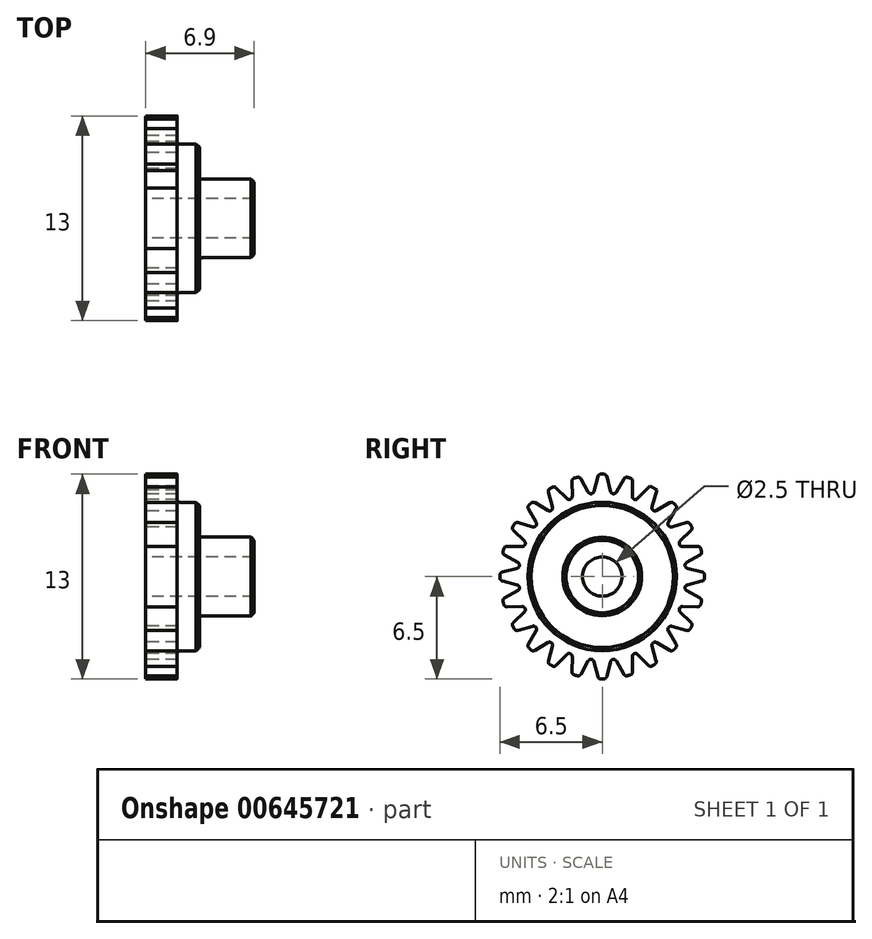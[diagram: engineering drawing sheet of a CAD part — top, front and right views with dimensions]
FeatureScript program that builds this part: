
annotation { "Feature Type Name" : "Feature", "Feature Type Description" : "" }
export const myFeature = defineFeature(function(context is Context, id is Id, definition is map)
    precondition{}
    {
        {
            var Q0;
            Q0=qCreatedBy(makeId("Front.planeOp"),FACE);
            var sketch = newSketch(context, id + "F0", { "sketchPlane" : qUnion([Q0])});
            skLineSegment(sketch, "E0", {"start": v(0, 1.25) * mm, "end": v(0, 6.5) * mm});
            skLineSegment(sketch, "E1", {"start": v(0, 6.5) * mm, "end": v(2, 6.5) * mm});
            skLineSegment(sketch, "E2", {"start": v(2, 6.5) * mm, "end": v(2, 4.72) * mm});
            skLineSegment(sketch, "E3", {"start": v(2, 4.71) * mm, "end": v(3.4, 4.72) * mm});
            skLineSegment(sketch, "E4", {"start": v(3.41, 4.72) * mm, "end": v(3.41, 2.5) * mm});
            skLineSegment(sketch, "E5", {"start": v(3.4, 2.5) * mm, "end": v(6.9, 2.5) * mm});
            skLineSegment(sketch, "E6", {"start": v(6.9, 2.5) * mm, "end": v(6.9, 1.25) * mm});
            skLineSegment(sketch, "E7", {"start": v(6.9, 1.25) * mm, "end": v(0, 1.25) * mm});
            skLineSegment(sketch, "E8", {"start": v(0, 0) * mm, "end": v(11.79, 0) * mm, "construction": true});
            skSolve(sketch);
        }
        {
            var Q0;
            Q0=makeQuery(id+"F0.imprint","IMPRINT",FACE,{"disambiguationData":[TD([[makeQuery(id+"F0.imprint","IMPRINT",EDGE,{"derivedFrom":sQuery(id+"F0.wireOp",EDGE,"E0")}),-1.0]])]});
            var Q1;
            Q1=sQuery(id+"F0.wireOp",EDGE,"E8");
            revolve(context, id + "F1", {"entities" : qUnion([Q0]), "axis" : qUnion([Q1]), "revolveType" : RevolveType.FULL});
        }
        {
            var Q0;
            Q0=makeQuery(id+"F1.opRevolve","SWEPT_FACE",FACE,{"disambiguationData":[OSD([sQuery(id+"F0.wireOp",EDGE,"E0")])]});
            var sketch = newSketch(context, id + "F2", { "sketchPlane" : qUnion([Q0])});
            skLineSegment(sketch, "E9", {"start": v(-0.25, 6.5) * mm, "end": v(-0.66, 4.87) * mm});
            skArc(sketch, "E10", {"start": v(0.25, 6.5) * mm, "mid": v(0, 6.5) * mm, "end": v(-0.25, 6.5) * mm});
            skLineSegment(sketch, "E11.MirrorCS", {"start": v(0.25, 6.5) * mm, "end": v(0.66, 4.87) * mm});
            skLineSegment(sketch, "E12.1.0", {"start": v(-1.92, 6.2) * mm, "end": v(-1.9, 4.53) * mm});
            skArc(sketch, "E12.1.1", {"start": v(-1.44, 6.34) * mm, "mid": v(-1.68, 6.28) * mm, "end": v(-1.92, 6.2) * mm});
            skLineSegment(sketch, "E12.1.2", {"start": v(-1.44, 6.34) * mm, "end": v(-0.62, 4.87) * mm});
            skLineSegment(sketch, "E12.2.0", {"start": v(-3.46, 5.5) * mm, "end": v(-3, 3.89) * mm});
            skArc(sketch, "E12.2.1", {"start": v(-3.03, 5.75) * mm, "mid": v(-3.25, 5.63) * mm, "end": v(-3.46, 5.5) * mm});
            skLineSegment(sketch, "E12.2.2", {"start": v(-3.03, 5.75) * mm, "end": v(-1.86, 4.55) * mm});
            skLineSegment(sketch, "E12.3.0", {"start": v(-4.77, 4.42) * mm, "end": v(-3.91, 2.97) * mm});
            skArc(sketch, "E12.3.1", {"start": v(-4.42, 4.77) * mm, "mid": v(-4.6, 4.6) * mm, "end": v(-4.77, 4.42) * mm});
            skLineSegment(sketch, "E12.3.2", {"start": v(-4.42, 4.77) * mm, "end": v(-2.97, 3.91) * mm});
            skLineSegment(sketch, "E12.4.0", {"start": v(-5.75, 3.03) * mm, "end": v(-4.55, 1.86) * mm});
            skArc(sketch, "E12.4.1", {"start": v(-5.5, 3.46) * mm, "mid": v(-5.63, 3.25) * mm, "end": v(-5.75, 3.03) * mm});
            skLineSegment(sketch, "E12.4.2", {"start": v(-5.5, 3.46) * mm, "end": v(-3.89, 3) * mm});
            skLineSegment(sketch, "E12.5.0", {"start": v(-6.34, 1.44) * mm, "end": v(-4.87, 0.62) * mm});
            skArc(sketch, "E12.5.1", {"start": v(-6.2, 1.92) * mm, "mid": v(-6.28, 1.68) * mm, "end": v(-6.34, 1.44) * mm});
            skLineSegment(sketch, "E12.5.2", {"start": v(-6.2, 1.92) * mm, "end": v(-4.53, 1.9) * mm});
            skLineSegment(sketch, "E12.6.0", {"start": v(-6.5, -0.25) * mm, "end": v(-4.87, -0.66) * mm});
            skArc(sketch, "E12.6.1", {"start": v(-6.5, 0.25) * mm, "mid": v(-6.5, 0) * mm, "end": v(-6.5, -0.25) * mm});
            skLineSegment(sketch, "E12.6.2", {"start": v(-6.5, 0.25) * mm, "end": v(-4.87, 0.66) * mm});
            skLineSegment(sketch, "E12.7.0", {"start": v(-6.2, -1.92) * mm, "end": v(-4.53, -1.9) * mm});
            skArc(sketch, "E12.7.1", {"start": v(-6.34, -1.44) * mm, "mid": v(-6.28, -1.68) * mm, "end": v(-6.2, -1.92) * mm});
            skLineSegment(sketch, "E12.7.2", {"start": v(-6.34, -1.44) * mm, "end": v(-4.87, -0.62) * mm});
            skLineSegment(sketch, "E12.8.0", {"start": v(-5.5, -3.46) * mm, "end": v(-3.89, -3) * mm});
            skArc(sketch, "E12.8.1", {"start": v(-5.75, -3.03) * mm, "mid": v(-5.63, -3.25) * mm, "end": v(-5.5, -3.46) * mm});
            skLineSegment(sketch, "E12.8.2", {"start": v(-5.75, -3.03) * mm, "end": v(-4.55, -1.86) * mm});
            skLineSegment(sketch, "E12.9.0", {"start": v(-4.42, -4.77) * mm, "end": v(-2.97, -3.91) * mm});
            skArc(sketch, "E12.9.1", {"start": v(-4.77, -4.42) * mm, "mid": v(-4.6, -4.6) * mm, "end": v(-4.42, -4.77) * mm});
            skLineSegment(sketch, "E12.9.2", {"start": v(-4.77, -4.42) * mm, "end": v(-3.91, -2.97) * mm});
            skLineSegment(sketch, "E12.10.0", {"start": v(-3.03, -5.75) * mm, "end": v(-1.86, -4.55) * mm});
            skArc(sketch, "E12.10.1", {"start": v(-3.46, -5.5) * mm, "mid": v(-3.25, -5.63) * mm, "end": v(-3.03, -5.75) * mm});
            skLineSegment(sketch, "E12.10.2", {"start": v(-3.46, -5.5) * mm, "end": v(-3, -3.89) * mm});
            skLineSegment(sketch, "E12.11.0", {"start": v(-1.44, -6.34) * mm, "end": v(-0.62, -4.87) * mm});
            skArc(sketch, "E12.11.1", {"start": v(-1.92, -6.2) * mm, "mid": v(-1.68, -6.28) * mm, "end": v(-1.44, -6.34) * mm});
            skLineSegment(sketch, "E12.11.2", {"start": v(-1.92, -6.2) * mm, "end": v(-1.9, -4.53) * mm});
            skLineSegment(sketch, "E12.12.0", {"start": v(0.25, -6.5) * mm, "end": v(0.66, -4.87) * mm});
            skArc(sketch, "E12.12.1", {"start": v(-0.25, -6.5) * mm, "mid": v(0, -6.5) * mm, "end": v(0.25, -6.5) * mm});
            skLineSegment(sketch, "E12.12.2", {"start": v(-0.25, -6.5) * mm, "end": v(-0.66, -4.87) * mm});
            skLineSegment(sketch, "E12.13.0", {"start": v(1.92, -6.2) * mm, "end": v(1.9, -4.53) * mm});
            skArc(sketch, "E12.13.1", {"start": v(1.44, -6.34) * mm, "mid": v(1.68, -6.28) * mm, "end": v(1.92, -6.2) * mm});
            skLineSegment(sketch, "E12.13.2", {"start": v(1.44, -6.34) * mm, "end": v(0.62, -4.87) * mm});
            skLineSegment(sketch, "E12.14.0", {"start": v(3.46, -5.5) * mm, "end": v(3, -3.89) * mm});
            skArc(sketch, "E12.14.1", {"start": v(3.03, -5.75) * mm, "mid": v(3.25, -5.63) * mm, "end": v(3.46, -5.5) * mm});
            skLineSegment(sketch, "E12.14.2", {"start": v(3.03, -5.75) * mm, "end": v(1.86, -4.55) * mm});
            skLineSegment(sketch, "E12.15.0", {"start": v(4.77, -4.42) * mm, "end": v(3.91, -2.97) * mm});
            skArc(sketch, "E12.15.1", {"start": v(4.42, -4.77) * mm, "mid": v(4.6, -4.6) * mm, "end": v(4.77, -4.42) * mm});
            skLineSegment(sketch, "E12.15.2", {"start": v(4.42, -4.77) * mm, "end": v(2.97, -3.91) * mm});
            skLineSegment(sketch, "E12.16.0", {"start": v(5.75, -3.03) * mm, "end": v(4.55, -1.86) * mm});
            skArc(sketch, "E12.16.1", {"start": v(5.5, -3.46) * mm, "mid": v(5.63, -3.25) * mm, "end": v(5.75, -3.03) * mm});
            skLineSegment(sketch, "E12.16.2", {"start": v(5.5, -3.46) * mm, "end": v(3.89, -3) * mm});
            skLineSegment(sketch, "E12.17.0", {"start": v(6.34, -1.44) * mm, "end": v(4.87, -0.62) * mm});
            skArc(sketch, "E12.17.1", {"start": v(6.2, -1.92) * mm, "mid": v(6.28, -1.68) * mm, "end": v(6.34, -1.44) * mm});
            skLineSegment(sketch, "E12.17.2", {"start": v(6.2, -1.92) * mm, "end": v(4.53, -1.9) * mm});
            skLineSegment(sketch, "E12.18.0", {"start": v(6.5, 0.25) * mm, "end": v(4.87, 0.66) * mm});
            skArc(sketch, "E12.18.1", {"start": v(6.5, -0.25) * mm, "mid": v(6.5, 0) * mm, "end": v(6.5, 0.25) * mm});
            skLineSegment(sketch, "E12.18.2", {"start": v(6.5, -0.25) * mm, "end": v(4.87, -0.66) * mm});
            skLineSegment(sketch, "E12.19.0", {"start": v(6.2, 1.92) * mm, "end": v(4.53, 1.9) * mm});
            skArc(sketch, "E12.19.1", {"start": v(6.34, 1.44) * mm, "mid": v(6.28, 1.68) * mm, "end": v(6.2, 1.92) * mm});
            skLineSegment(sketch, "E12.19.2", {"start": v(6.34, 1.44) * mm, "end": v(4.87, 0.62) * mm});
            skLineSegment(sketch, "E12.20.0", {"start": v(5.5, 3.46) * mm, "end": v(3.89, 3) * mm});
            skArc(sketch, "E12.20.1", {"start": v(5.75, 3.03) * mm, "mid": v(5.63, 3.25) * mm, "end": v(5.5, 3.46) * mm});
            skLineSegment(sketch, "E12.20.2", {"start": v(5.75, 3.03) * mm, "end": v(4.55, 1.86) * mm});
            skLineSegment(sketch, "E12.21.0", {"start": v(4.42, 4.77) * mm, "end": v(2.97, 3.91) * mm});
            skArc(sketch, "E12.21.1", {"start": v(4.77, 4.42) * mm, "mid": v(4.6, 4.6) * mm, "end": v(4.42, 4.77) * mm});
            skLineSegment(sketch, "E12.21.2", {"start": v(4.77, 4.42) * mm, "end": v(3.91, 2.97) * mm});
            skLineSegment(sketch, "E12.22.0", {"start": v(3.03, 5.75) * mm, "end": v(1.86, 4.55) * mm});
            skArc(sketch, "E12.22.1", {"start": v(3.46, 5.5) * mm, "mid": v(3.25, 5.63) * mm, "end": v(3.03, 5.75) * mm});
            skLineSegment(sketch, "E12.22.2", {"start": v(3.46, 5.5) * mm, "end": v(3, 3.89) * mm});
            skLineSegment(sketch, "E12.23.0", {"start": v(1.44, 6.34) * mm, "end": v(0.62, 4.87) * mm});
            skArc(sketch, "E12.23.1", {"start": v(1.92, 6.2) * mm, "mid": v(1.68, 6.28) * mm, "end": v(1.44, 6.34) * mm});
            skLineSegment(sketch, "E12.23.2", {"start": v(1.92, 6.2) * mm, "end": v(1.9, 4.53) * mm});
            skCircle(sketch, "E13", {"center": v(0, 0) * mm, "radius": 7.21 * mm});
            skSolve(sketch);
        }
        {
            var Q0;
            {var subQ0=sQuery(id+"F2.wireOp",EDGE,"E12.2.0");var subQ3=sQuery(id+"F2.wireOp",EDGE,"E12.3.2");var subQ4=makeQuery(id+"F2.imprint","INTERSECT",VERTEX,{"derivedFrom":[subQ0,subQ3]});Q0=makeQuery(id+"F2.imprint","IMPRINT",FACE,{"disambiguationData":[TD([[makeQuery(id+"F2.imprint","IMPRINT",EDGE,{"disambiguationData":[TD([[subQ4,1.0]])],"derivedFrom":subQ0}),-1.0]])]});}
            var Q1;
            {var subQ0=sQuery(id+"F2.wireOp",EDGE,"E12.1.0");var subQ3=sQuery(id+"F2.wireOp",EDGE,"E12.2.2");var subQ4=makeQuery(id+"F2.imprint","INTERSECT",VERTEX,{"derivedFrom":[subQ0,subQ3]});Q1=makeQuery(id+"F2.imprint","IMPRINT",FACE,{"disambiguationData":[TD([[makeQuery(id+"F2.imprint","IMPRINT",EDGE,{"disambiguationData":[TD([[subQ4,1.0]])],"derivedFrom":subQ0}),-1.0]])]});}
            var Q2;
            {var subQ0=sQuery(id+"F2.wireOp",EDGE,"E9");var subQ3=sQuery(id+"F2.wireOp",EDGE,"E12.1.2");var subQ4=makeQuery(id+"F2.imprint","INTERSECT",VERTEX,{"derivedFrom":[subQ0,subQ3]});Q2=makeQuery(id+"F2.imprint","IMPRINT",FACE,{"disambiguationData":[TD([[makeQuery(id+"F2.imprint","IMPRINT",EDGE,{"disambiguationData":[TD([[subQ4,1.0]])],"derivedFrom":subQ0}),-1.0]])]});}
            var Q3;
            {var subQ0=sQuery(id+"F2.wireOp",EDGE,"E11.MirrorCS");var subQ3=sQuery(id+"F2.wireOp",EDGE,"E12.23.0");var subQ4=makeQuery(id+"F2.imprint","INTERSECT",VERTEX,{"derivedFrom":[subQ0,subQ3]});Q3=makeQuery(id+"F2.imprint","IMPRINT",FACE,{"disambiguationData":[TD([[makeQuery(id+"F2.imprint","IMPRINT",EDGE,{"disambiguationData":[TD([[subQ4,1.0]])],"derivedFrom":subQ0}),1.0]])]});}
            var Q4;
            {var subQ0=sQuery(id+"F2.wireOp",EDGE,"E12.22.0");var subQ3=sQuery(id+"F2.wireOp",EDGE,"E12.23.2");var subQ4=makeQuery(id+"F2.imprint","INTERSECT",VERTEX,{"derivedFrom":[subQ0,subQ3]});Q4=makeQuery(id+"F2.imprint","IMPRINT",FACE,{"disambiguationData":[TD([[makeQuery(id+"F2.imprint","IMPRINT",EDGE,{"disambiguationData":[TD([[subQ4,1.0]])],"derivedFrom":subQ0}),-1.0]])]});}
            var Q5;
            {var subQ0=sQuery(id+"F2.wireOp",EDGE,"E12.21.0");var subQ3=sQuery(id+"F2.wireOp",EDGE,"E12.22.2");var subQ4=makeQuery(id+"F2.imprint","INTERSECT",VERTEX,{"derivedFrom":[subQ0,subQ3]});Q5=makeQuery(id+"F2.imprint","IMPRINT",FACE,{"disambiguationData":[TD([[makeQuery(id+"F2.imprint","IMPRINT",EDGE,{"disambiguationData":[TD([[subQ4,1.0]])],"derivedFrom":subQ0}),-1.0]])]});}
            var Q6;
            {var subQ0=sQuery(id+"F2.wireOp",EDGE,"E12.20.0");var subQ3=sQuery(id+"F2.wireOp",EDGE,"E12.21.2");var subQ4=makeQuery(id+"F2.imprint","INTERSECT",VERTEX,{"derivedFrom":[subQ0,subQ3]});Q6=makeQuery(id+"F2.imprint","IMPRINT",FACE,{"disambiguationData":[TD([[makeQuery(id+"F2.imprint","IMPRINT",EDGE,{"disambiguationData":[TD([[subQ4,1.0]])],"derivedFrom":subQ0}),-1.0]])]});}
            var Q7;
            {var subQ0=sQuery(id+"F2.wireOp",EDGE,"E12.19.0");var subQ3=sQuery(id+"F2.wireOp",EDGE,"E12.20.2");var subQ4=makeQuery(id+"F2.imprint","INTERSECT",VERTEX,{"derivedFrom":[subQ0,subQ3]});Q7=makeQuery(id+"F2.imprint","IMPRINT",FACE,{"disambiguationData":[TD([[makeQuery(id+"F2.imprint","IMPRINT",EDGE,{"disambiguationData":[TD([[subQ4,1.0]])],"derivedFrom":subQ0}),-1.0]])]});}
            var Q8;
            {var subQ0=sQuery(id+"F2.wireOp",EDGE,"E12.18.0");var subQ3=sQuery(id+"F2.wireOp",EDGE,"E12.19.2");var subQ4=makeQuery(id+"F2.imprint","INTERSECT",VERTEX,{"derivedFrom":[subQ0,subQ3]});Q8=makeQuery(id+"F2.imprint","IMPRINT",FACE,{"disambiguationData":[TD([[makeQuery(id+"F2.imprint","IMPRINT",EDGE,{"disambiguationData":[TD([[subQ4,1.0]])],"derivedFrom":subQ0}),-1.0]])]});}
            var Q9;
            {var subQ0=sQuery(id+"F2.wireOp",EDGE,"E12.17.0");var subQ3=sQuery(id+"F2.wireOp",EDGE,"E12.18.2");var subQ4=makeQuery(id+"F2.imprint","INTERSECT",VERTEX,{"derivedFrom":[subQ0,subQ3]});Q9=makeQuery(id+"F2.imprint","IMPRINT",FACE,{"disambiguationData":[TD([[makeQuery(id+"F2.imprint","IMPRINT",EDGE,{"disambiguationData":[TD([[subQ4,1.0]])],"derivedFrom":subQ0}),-1.0]])]});}
            var Q10;
            {var subQ0=sQuery(id+"F2.wireOp",EDGE,"E12.16.0");var subQ3=sQuery(id+"F2.wireOp",EDGE,"E12.17.2");var subQ4=makeQuery(id+"F2.imprint","INTERSECT",VERTEX,{"derivedFrom":[subQ0,subQ3]});Q10=makeQuery(id+"F2.imprint","IMPRINT",FACE,{"disambiguationData":[TD([[makeQuery(id+"F2.imprint","IMPRINT",EDGE,{"disambiguationData":[TD([[subQ4,1.0]])],"derivedFrom":subQ0}),-1.0]])]});}
            var Q11;
            {var subQ0=sQuery(id+"F2.wireOp",EDGE,"E12.15.0");var subQ3=sQuery(id+"F2.wireOp",EDGE,"E12.16.2");var subQ4=makeQuery(id+"F2.imprint","INTERSECT",VERTEX,{"derivedFrom":[subQ0,subQ3]});Q11=makeQuery(id+"F2.imprint","IMPRINT",FACE,{"disambiguationData":[TD([[makeQuery(id+"F2.imprint","IMPRINT",EDGE,{"disambiguationData":[TD([[subQ4,1.0]])],"derivedFrom":subQ0}),-1.0]])]});}
            var Q12;
            {var subQ0=sQuery(id+"F2.wireOp",EDGE,"E12.14.0");var subQ3=sQuery(id+"F2.wireOp",EDGE,"E12.15.2");var subQ4=makeQuery(id+"F2.imprint","INTERSECT",VERTEX,{"derivedFrom":[subQ0,subQ3]});Q12=makeQuery(id+"F2.imprint","IMPRINT",FACE,{"disambiguationData":[TD([[makeQuery(id+"F2.imprint","IMPRINT",EDGE,{"disambiguationData":[TD([[subQ4,1.0]])],"derivedFrom":subQ0}),-1.0]])]});}
            var Q13;
            {var subQ0=sQuery(id+"F2.wireOp",EDGE,"E12.13.0");var subQ3=sQuery(id+"F2.wireOp",EDGE,"E12.14.2");var subQ4=makeQuery(id+"F2.imprint","INTERSECT",VERTEX,{"derivedFrom":[subQ0,subQ3]});Q13=makeQuery(id+"F2.imprint","IMPRINT",FACE,{"disambiguationData":[TD([[makeQuery(id+"F2.imprint","IMPRINT",EDGE,{"disambiguationData":[TD([[subQ4,1.0]])],"derivedFrom":subQ0}),-1.0]])]});}
            var Q14;
            {var subQ0=sQuery(id+"F2.wireOp",EDGE,"E12.12.0");var subQ3=sQuery(id+"F2.wireOp",EDGE,"E12.13.2");var subQ4=makeQuery(id+"F2.imprint","INTERSECT",VERTEX,{"derivedFrom":[subQ0,subQ3]});Q14=makeQuery(id+"F2.imprint","IMPRINT",FACE,{"disambiguationData":[TD([[makeQuery(id+"F2.imprint","IMPRINT",EDGE,{"disambiguationData":[TD([[subQ4,1.0]])],"derivedFrom":subQ0}),-1.0]])]});}
            var Q15;
            {var subQ0=sQuery(id+"F2.wireOp",EDGE,"E12.11.0");var subQ3=sQuery(id+"F2.wireOp",EDGE,"E12.12.2");var subQ4=makeQuery(id+"F2.imprint","INTERSECT",VERTEX,{"derivedFrom":[subQ0,subQ3]});Q15=makeQuery(id+"F2.imprint","IMPRINT",FACE,{"disambiguationData":[TD([[makeQuery(id+"F2.imprint","IMPRINT",EDGE,{"disambiguationData":[TD([[subQ4,1.0]])],"derivedFrom":subQ0}),-1.0]])]});}
            var Q16;
            {var subQ0=sQuery(id+"F2.wireOp",EDGE,"E12.10.0");var subQ3=sQuery(id+"F2.wireOp",EDGE,"E12.11.2");var subQ4=makeQuery(id+"F2.imprint","INTERSECT",VERTEX,{"derivedFrom":[subQ0,subQ3]});Q16=makeQuery(id+"F2.imprint","IMPRINT",FACE,{"disambiguationData":[TD([[makeQuery(id+"F2.imprint","IMPRINT",EDGE,{"disambiguationData":[TD([[subQ4,1.0]])],"derivedFrom":subQ0}),-1.0]])]});}
            var Q17;
            {var subQ0=sQuery(id+"F2.wireOp",EDGE,"E12.9.0");var subQ3=sQuery(id+"F2.wireOp",EDGE,"E12.10.2");var subQ4=makeQuery(id+"F2.imprint","INTERSECT",VERTEX,{"derivedFrom":[subQ0,subQ3]});Q17=makeQuery(id+"F2.imprint","IMPRINT",FACE,{"disambiguationData":[TD([[makeQuery(id+"F2.imprint","IMPRINT",EDGE,{"disambiguationData":[TD([[subQ4,1.0]])],"derivedFrom":subQ0}),-1.0]])]});}
            var Q18;
            {var subQ0=sQuery(id+"F2.wireOp",EDGE,"E12.8.0");var subQ3=sQuery(id+"F2.wireOp",EDGE,"E12.9.2");var subQ4=makeQuery(id+"F2.imprint","INTERSECT",VERTEX,{"derivedFrom":[subQ0,subQ3]});Q18=makeQuery(id+"F2.imprint","IMPRINT",FACE,{"disambiguationData":[TD([[makeQuery(id+"F2.imprint","IMPRINT",EDGE,{"disambiguationData":[TD([[subQ4,1.0]])],"derivedFrom":subQ0}),-1.0]])]});}
            var Q19;
            {var subQ0=sQuery(id+"F2.wireOp",EDGE,"E12.7.0");var subQ3=sQuery(id+"F2.wireOp",EDGE,"E12.8.2");var subQ4=makeQuery(id+"F2.imprint","INTERSECT",VERTEX,{"derivedFrom":[subQ0,subQ3]});Q19=makeQuery(id+"F2.imprint","IMPRINT",FACE,{"disambiguationData":[TD([[makeQuery(id+"F2.imprint","IMPRINT",EDGE,{"disambiguationData":[TD([[subQ4,1.0]])],"derivedFrom":subQ0}),-1.0]])]});}
            var Q20;
            {var subQ0=sQuery(id+"F2.wireOp",EDGE,"E12.6.0");var subQ3=sQuery(id+"F2.wireOp",EDGE,"E12.7.2");var subQ4=makeQuery(id+"F2.imprint","INTERSECT",VERTEX,{"derivedFrom":[subQ0,subQ3]});Q20=makeQuery(id+"F2.imprint","IMPRINT",FACE,{"disambiguationData":[TD([[makeQuery(id+"F2.imprint","IMPRINT",EDGE,{"disambiguationData":[TD([[subQ4,1.0]])],"derivedFrom":subQ0}),-1.0]])]});}
            var Q21;
            {var subQ0=sQuery(id+"F2.wireOp",EDGE,"E12.5.0");var subQ3=sQuery(id+"F2.wireOp",EDGE,"E12.6.2");var subQ4=makeQuery(id+"F2.imprint","INTERSECT",VERTEX,{"derivedFrom":[subQ0,subQ3]});Q21=makeQuery(id+"F2.imprint","IMPRINT",FACE,{"disambiguationData":[TD([[makeQuery(id+"F2.imprint","IMPRINT",EDGE,{"disambiguationData":[TD([[subQ4,1.0]])],"derivedFrom":subQ0}),-1.0]])]});}
            var Q22;
            {var subQ0=sQuery(id+"F2.wireOp",EDGE,"E12.4.0");var subQ3=sQuery(id+"F2.wireOp",EDGE,"E12.5.2");var subQ4=makeQuery(id+"F2.imprint","INTERSECT",VERTEX,{"derivedFrom":[subQ0,subQ3]});Q22=makeQuery(id+"F2.imprint","IMPRINT",FACE,{"disambiguationData":[TD([[makeQuery(id+"F2.imprint","IMPRINT",EDGE,{"disambiguationData":[TD([[subQ4,1.0]])],"derivedFrom":subQ0}),-1.0]])]});}
            var Q23;
            {var subQ0=sQuery(id+"F2.wireOp",EDGE,"E12.3.0");var subQ3=sQuery(id+"F2.wireOp",EDGE,"E12.4.2");var subQ4=makeQuery(id+"F2.imprint","INTERSECT",VERTEX,{"derivedFrom":[subQ0,subQ3]});Q23=makeQuery(id+"F2.imprint","IMPRINT",FACE,{"disambiguationData":[TD([[makeQuery(id+"F2.imprint","IMPRINT",EDGE,{"disambiguationData":[TD([[subQ4,1.0]])],"derivedFrom":subQ0}),-1.0]])]});}
            extrude(context, id + "F3", {"entities" : qUnion([Q0, Q1, Q2, Q3, Q4, Q5, Q6, Q7, Q8, Q9, Q10, Q11, Q12, Q13, Q14, Q15, Q16, Q17, Q18, Q19, Q20, Q21, Q22, Q23]), "operationType" : NewBodyOperationType.REMOVE, "oppositeDirection" : true, "depth" : 25 * mm, "offsetDistance" : 25 * mm});
        }
        {
            var Q0;
            Q0=makeQuery(id+"F3.boolean.opBoolean","COPY",EDGE,{"derivedFrom":makeQuery(id+"F3.opExtrude","SWEPT_EDGE",EDGE,{"disambiguationData":[OSD([sQuery(id+"F2.wireOp",EDGE,"E12.2.0"),sQuery(id+"F2.wireOp",EDGE,"E12.3.2")])]})});
            var Q1;
            Q1=makeQuery(id+"F3.boolean.opBoolean","COPY",EDGE,{"derivedFrom":makeQuery(id+"F3.opExtrude","SWEPT_EDGE",EDGE,{"disambiguationData":[OSD([sQuery(id+"F2.wireOp",EDGE,"E12.1.0"),sQuery(id+"F2.wireOp",EDGE,"E12.2.2")])]})});
            var Q2;
            Q2=makeQuery(id+"F3.boolean.opBoolean","COPY",EDGE,{"derivedFrom":makeQuery(id+"F3.opExtrude","SWEPT_EDGE",EDGE,{"disambiguationData":[OSD([sQuery(id+"F2.wireOp",EDGE,"E9"),sQuery(id+"F2.wireOp",EDGE,"E12.1.2")])]})});
            var Q3;
            Q3=makeQuery(id+"F3.boolean.opBoolean","COPY",EDGE,{"derivedFrom":makeQuery(id+"F3.opExtrude","SWEPT_EDGE",EDGE,{"disambiguationData":[OSD([sQuery(id+"F2.wireOp",EDGE,"E11.MirrorCS"),sQuery(id+"F2.wireOp",EDGE,"E12.23.0")])]})});
            var Q4;
            Q4=makeQuery(id+"F3.boolean.opBoolean","COPY",EDGE,{"derivedFrom":makeQuery(id+"F3.opExtrude","SWEPT_EDGE",EDGE,{"disambiguationData":[OSD([sQuery(id+"F2.wireOp",EDGE,"E12.22.0"),sQuery(id+"F2.wireOp",EDGE,"E12.23.2")])]})});
            var Q5;
            Q5=makeQuery(id+"F3.boolean.opBoolean","COPY",EDGE,{"derivedFrom":makeQuery(id+"F3.opExtrude","SWEPT_EDGE",EDGE,{"disambiguationData":[OSD([sQuery(id+"F2.wireOp",EDGE,"E12.21.0"),sQuery(id+"F2.wireOp",EDGE,"E12.22.2")])]})});
            var Q6;
            Q6=makeQuery(id+"F3.boolean.opBoolean","COPY",EDGE,{"derivedFrom":makeQuery(id+"F3.opExtrude","SWEPT_EDGE",EDGE,{"disambiguationData":[OSD([sQuery(id+"F2.wireOp",EDGE,"E12.20.0"),sQuery(id+"F2.wireOp",EDGE,"E12.21.2")])]})});
            var Q7;
            Q7=makeQuery(id+"F3.boolean.opBoolean","COPY",EDGE,{"derivedFrom":makeQuery(id+"F3.opExtrude","SWEPT_EDGE",EDGE,{"disambiguationData":[OSD([sQuery(id+"F2.wireOp",EDGE,"E12.19.0"),sQuery(id+"F2.wireOp",EDGE,"E12.20.2")])]})});
            var Q8;
            Q8=makeQuery(id+"F3.boolean.opBoolean","COPY",EDGE,{"derivedFrom":makeQuery(id+"F3.opExtrude","SWEPT_EDGE",EDGE,{"disambiguationData":[OSD([sQuery(id+"F2.wireOp",EDGE,"E12.18.0"),sQuery(id+"F2.wireOp",EDGE,"E12.19.2")])]})});
            var Q9;
            Q9=makeQuery(id+"F3.boolean.opBoolean","COPY",EDGE,{"derivedFrom":makeQuery(id+"F3.opExtrude","SWEPT_EDGE",EDGE,{"disambiguationData":[OSD([sQuery(id+"F2.wireOp",EDGE,"E12.17.0"),sQuery(id+"F2.wireOp",EDGE,"E12.18.2")])]})});
            var Q10;
            Q10=makeQuery(id+"F3.boolean.opBoolean","COPY",EDGE,{"derivedFrom":makeQuery(id+"F3.opExtrude","SWEPT_EDGE",EDGE,{"disambiguationData":[OSD([sQuery(id+"F2.wireOp",EDGE,"E12.16.0"),sQuery(id+"F2.wireOp",EDGE,"E12.17.2")])]})});
            var Q11;
            Q11=makeQuery(id+"F3.boolean.opBoolean","COPY",EDGE,{"derivedFrom":makeQuery(id+"F3.opExtrude","SWEPT_EDGE",EDGE,{"disambiguationData":[OSD([sQuery(id+"F2.wireOp",EDGE,"E12.15.0"),sQuery(id+"F2.wireOp",EDGE,"E12.16.2")])]})});
            var Q12;
            Q12=makeQuery(id+"F3.boolean.opBoolean","COPY",EDGE,{"derivedFrom":makeQuery(id+"F3.opExtrude","SWEPT_EDGE",EDGE,{"disambiguationData":[OSD([sQuery(id+"F2.wireOp",EDGE,"E12.14.0"),sQuery(id+"F2.wireOp",EDGE,"E12.15.2")])]})});
            var Q13;
            Q13=makeQuery(id+"F3.boolean.opBoolean","COPY",EDGE,{"derivedFrom":makeQuery(id+"F3.opExtrude","SWEPT_EDGE",EDGE,{"disambiguationData":[OSD([sQuery(id+"F2.wireOp",EDGE,"E12.13.0"),sQuery(id+"F2.wireOp",EDGE,"E12.14.2")])]})});
            var Q14;
            Q14=makeQuery(id+"F3.boolean.opBoolean","COPY",EDGE,{"derivedFrom":makeQuery(id+"F3.opExtrude","SWEPT_EDGE",EDGE,{"disambiguationData":[OSD([sQuery(id+"F2.wireOp",EDGE,"E12.12.0"),sQuery(id+"F2.wireOp",EDGE,"E12.13.2")])]})});
            var Q15;
            Q15=makeQuery(id+"F3.boolean.opBoolean","COPY",EDGE,{"derivedFrom":makeQuery(id+"F3.opExtrude","SWEPT_EDGE",EDGE,{"disambiguationData":[OSD([sQuery(id+"F2.wireOp",EDGE,"E12.11.0"),sQuery(id+"F2.wireOp",EDGE,"E12.12.2")])]})});
            var Q16;
            Q16=makeQuery(id+"F3.boolean.opBoolean","COPY",EDGE,{"derivedFrom":makeQuery(id+"F3.opExtrude","SWEPT_EDGE",EDGE,{"disambiguationData":[OSD([sQuery(id+"F2.wireOp",EDGE,"E12.10.0"),sQuery(id+"F2.wireOp",EDGE,"E12.11.2")])]})});
            var Q17;
            Q17=makeQuery(id+"F3.boolean.opBoolean","COPY",EDGE,{"derivedFrom":makeQuery(id+"F3.opExtrude","SWEPT_EDGE",EDGE,{"disambiguationData":[OSD([sQuery(id+"F2.wireOp",EDGE,"E12.9.0"),sQuery(id+"F2.wireOp",EDGE,"E12.10.2")])]})});
            var Q18;
            Q18=makeQuery(id+"F3.boolean.opBoolean","COPY",EDGE,{"derivedFrom":makeQuery(id+"F3.opExtrude","SWEPT_EDGE",EDGE,{"disambiguationData":[OSD([sQuery(id+"F2.wireOp",EDGE,"E12.8.0"),sQuery(id+"F2.wireOp",EDGE,"E12.9.2")])]})});
            var Q19;
            Q19=makeQuery(id+"F3.boolean.opBoolean","COPY",EDGE,{"derivedFrom":makeQuery(id+"F3.opExtrude","SWEPT_EDGE",EDGE,{"disambiguationData":[OSD([sQuery(id+"F2.wireOp",EDGE,"E12.7.0"),sQuery(id+"F2.wireOp",EDGE,"E12.8.2")])]})});
            var Q20;
            Q20=makeQuery(id+"F3.boolean.opBoolean","COPY",EDGE,{"derivedFrom":makeQuery(id+"F3.opExtrude","SWEPT_EDGE",EDGE,{"disambiguationData":[OSD([sQuery(id+"F2.wireOp",EDGE,"E12.6.0"),sQuery(id+"F2.wireOp",EDGE,"E12.7.2")])]})});
            var Q21;
            Q21=makeQuery(id+"F3.boolean.opBoolean","COPY",EDGE,{"derivedFrom":makeQuery(id+"F3.opExtrude","SWEPT_EDGE",EDGE,{"disambiguationData":[OSD([sQuery(id+"F2.wireOp",EDGE,"E12.5.0"),sQuery(id+"F2.wireOp",EDGE,"E12.6.2")])]})});
            var Q22;
            Q22=makeQuery(id+"F3.boolean.opBoolean","COPY",EDGE,{"derivedFrom":makeQuery(id+"F3.opExtrude","SWEPT_EDGE",EDGE,{"disambiguationData":[OSD([sQuery(id+"F2.wireOp",EDGE,"E12.4.0"),sQuery(id+"F2.wireOp",EDGE,"E12.5.2")])]})});
            var Q23;
            Q23=makeQuery(id+"F3.boolean.opBoolean","COPY",EDGE,{"derivedFrom":makeQuery(id+"F3.opExtrude","SWEPT_EDGE",EDGE,{"disambiguationData":[OSD([sQuery(id+"F2.wireOp",EDGE,"E12.3.0"),sQuery(id+"F2.wireOp",EDGE,"E12.4.2")])]})});
            fillet(context, id + "F4", {"entities" : qUnion([Q0, Q1, Q2, Q3, Q4, Q5, Q6, Q7, Q8, Q9, Q10, Q11, Q12, Q13, Q14, Q15, Q16, Q17, Q18, Q19, Q20, Q21, Q22, Q23]), "radius" : 0.2 * mm, "tangentPropagation" : true, "allowEdgeOverflow" : false});
        }
        {
            var Q0;
            Q0=makeQuery(id+"F3.boolean.opBoolean","COPY",EDGE,{"derivedFrom":makeQuery(id+"F3.opExtrude","SWEPT_EDGE",EDGE,{"disambiguationData":[OSD([sQuery(id+"F0.wireOp",EDGE,"E0"),sQuery(id+"F0.wireOp",EDGE,"E1"),sQuery(id+"F2.wireOp",EDGE,"E12.22.0"),sQuery(id+"F2.wireOp",EDGE,"E12.22.1")])]})});
            var Q1;
            Q1=makeQuery(id+"F3.boolean.opBoolean","COPY",EDGE,{"derivedFrom":makeQuery(id+"F3.opExtrude","SWEPT_EDGE",EDGE,{"disambiguationData":[OSD([sQuery(id+"F0.wireOp",EDGE,"E0"),sQuery(id+"F0.wireOp",EDGE,"E1"),sQuery(id+"F2.wireOp",EDGE,"E12.22.1"),sQuery(id+"F2.wireOp",EDGE,"E12.22.2")])]})});
            var Q2;
            Q2=makeQuery(id+"F3.boolean.opBoolean","COPY",EDGE,{"derivedFrom":makeQuery(id+"F3.opExtrude","SWEPT_EDGE",EDGE,{"disambiguationData":[OSD([sQuery(id+"F0.wireOp",EDGE,"E0"),sQuery(id+"F0.wireOp",EDGE,"E1"),sQuery(id+"F2.wireOp",EDGE,"E12.21.0"),sQuery(id+"F2.wireOp",EDGE,"E12.21.1")])]})});
            var Q3;
            Q3=makeQuery(id+"F3.boolean.opBoolean","COPY",EDGE,{"derivedFrom":makeQuery(id+"F3.opExtrude","SWEPT_EDGE",EDGE,{"disambiguationData":[OSD([sQuery(id+"F0.wireOp",EDGE,"E0"),sQuery(id+"F0.wireOp",EDGE,"E1"),sQuery(id+"F2.wireOp",EDGE,"E12.21.1"),sQuery(id+"F2.wireOp",EDGE,"E12.21.2")])]})});
            var Q4;
            Q4=makeQuery(id+"F3.boolean.opBoolean","COPY",EDGE,{"derivedFrom":makeQuery(id+"F3.opExtrude","SWEPT_EDGE",EDGE,{"disambiguationData":[OSD([sQuery(id+"F0.wireOp",EDGE,"E0"),sQuery(id+"F0.wireOp",EDGE,"E1"),sQuery(id+"F2.wireOp",EDGE,"E12.20.0"),sQuery(id+"F2.wireOp",EDGE,"E12.20.1")])]})});
            var Q5;
            Q5=makeQuery(id+"F3.boolean.opBoolean","COPY",EDGE,{"derivedFrom":makeQuery(id+"F3.opExtrude","SWEPT_EDGE",EDGE,{"disambiguationData":[OSD([sQuery(id+"F0.wireOp",EDGE,"E0"),sQuery(id+"F0.wireOp",EDGE,"E1"),sQuery(id+"F2.wireOp",EDGE,"E12.20.1"),sQuery(id+"F2.wireOp",EDGE,"E12.20.2")])]})});
            var Q6;
            Q6=makeQuery(id+"F3.boolean.opBoolean","COPY",EDGE,{"derivedFrom":makeQuery(id+"F3.opExtrude","SWEPT_EDGE",EDGE,{"disambiguationData":[OSD([sQuery(id+"F0.wireOp",EDGE,"E0"),sQuery(id+"F0.wireOp",EDGE,"E1"),sQuery(id+"F2.wireOp",EDGE,"E12.19.0"),sQuery(id+"F2.wireOp",EDGE,"E12.19.1")])]})});
            var Q7;
            Q7=makeQuery(id+"F3.boolean.opBoolean","COPY",EDGE,{"derivedFrom":makeQuery(id+"F3.opExtrude","SWEPT_EDGE",EDGE,{"disambiguationData":[OSD([sQuery(id+"F0.wireOp",EDGE,"E0"),sQuery(id+"F0.wireOp",EDGE,"E1"),sQuery(id+"F2.wireOp",EDGE,"E12.19.1"),sQuery(id+"F2.wireOp",EDGE,"E12.19.2")])]})});
            var Q8;
            Q8=makeQuery(id+"F3.boolean.opBoolean","COPY",EDGE,{"derivedFrom":makeQuery(id+"F3.opExtrude","SWEPT_EDGE",EDGE,{"disambiguationData":[OSD([sQuery(id+"F0.wireOp",EDGE,"E0"),sQuery(id+"F0.wireOp",EDGE,"E1"),sQuery(id+"F2.wireOp",EDGE,"E12.18.0"),sQuery(id+"F2.wireOp",EDGE,"E12.18.1")])]})});
            var Q9;
            Q9=makeQuery(id+"F3.boolean.opBoolean","COPY",EDGE,{"derivedFrom":makeQuery(id+"F3.opExtrude","SWEPT_EDGE",EDGE,{"disambiguationData":[OSD([sQuery(id+"F0.wireOp",EDGE,"E0"),sQuery(id+"F0.wireOp",EDGE,"E1"),sQuery(id+"F2.wireOp",EDGE,"E12.18.1"),sQuery(id+"F2.wireOp",EDGE,"E12.18.2")])]})});
            var Q10;
            Q10=makeQuery(id+"F3.boolean.opBoolean","COPY",EDGE,{"derivedFrom":makeQuery(id+"F3.opExtrude","SWEPT_EDGE",EDGE,{"disambiguationData":[OSD([sQuery(id+"F0.wireOp",EDGE,"E0"),sQuery(id+"F0.wireOp",EDGE,"E1"),sQuery(id+"F2.wireOp",EDGE,"E12.17.0"),sQuery(id+"F2.wireOp",EDGE,"E12.17.1")])]})});
            var Q11;
            Q11=makeQuery(id+"F3.boolean.opBoolean","COPY",EDGE,{"derivedFrom":makeQuery(id+"F3.opExtrude","SWEPT_EDGE",EDGE,{"disambiguationData":[OSD([sQuery(id+"F0.wireOp",EDGE,"E0"),sQuery(id+"F0.wireOp",EDGE,"E1"),sQuery(id+"F2.wireOp",EDGE,"E12.17.1"),sQuery(id+"F2.wireOp",EDGE,"E12.17.2")])]})});
            var Q12;
            Q12=makeQuery(id+"F3.boolean.opBoolean","COPY",EDGE,{"derivedFrom":makeQuery(id+"F3.opExtrude","SWEPT_EDGE",EDGE,{"disambiguationData":[OSD([sQuery(id+"F0.wireOp",EDGE,"E0"),sQuery(id+"F0.wireOp",EDGE,"E1"),sQuery(id+"F2.wireOp",EDGE,"E12.16.0"),sQuery(id+"F2.wireOp",EDGE,"E12.16.1")])]})});
            var Q13;
            Q13=makeQuery(id+"F3.boolean.opBoolean","COPY",EDGE,{"derivedFrom":makeQuery(id+"F3.opExtrude","SWEPT_EDGE",EDGE,{"disambiguationData":[OSD([sQuery(id+"F0.wireOp",EDGE,"E0"),sQuery(id+"F0.wireOp",EDGE,"E1"),sQuery(id+"F2.wireOp",EDGE,"E12.16.1"),sQuery(id+"F2.wireOp",EDGE,"E12.16.2")])]})});
            var Q14;
            Q14=makeQuery(id+"F3.boolean.opBoolean","COPY",EDGE,{"derivedFrom":makeQuery(id+"F3.opExtrude","SWEPT_EDGE",EDGE,{"disambiguationData":[OSD([sQuery(id+"F0.wireOp",EDGE,"E0"),sQuery(id+"F0.wireOp",EDGE,"E1"),sQuery(id+"F2.wireOp",EDGE,"E12.15.0"),sQuery(id+"F2.wireOp",EDGE,"E12.15.1")])]})});
            var Q15;
            Q15=makeQuery(id+"F3.boolean.opBoolean","COPY",EDGE,{"derivedFrom":makeQuery(id+"F3.opExtrude","SWEPT_EDGE",EDGE,{"disambiguationData":[OSD([sQuery(id+"F0.wireOp",EDGE,"E0"),sQuery(id+"F0.wireOp",EDGE,"E1"),sQuery(id+"F2.wireOp",EDGE,"E12.15.1"),sQuery(id+"F2.wireOp",EDGE,"E12.15.2")])]})});
            var Q16;
            Q16=makeQuery(id+"F3.boolean.opBoolean","COPY",EDGE,{"derivedFrom":makeQuery(id+"F3.opExtrude","SWEPT_EDGE",EDGE,{"disambiguationData":[OSD([sQuery(id+"F0.wireOp",EDGE,"E0"),sQuery(id+"F0.wireOp",EDGE,"E1"),sQuery(id+"F2.wireOp",EDGE,"E12.14.0"),sQuery(id+"F2.wireOp",EDGE,"E12.14.1")])]})});
            var Q17;
            Q17=makeQuery(id+"F3.boolean.opBoolean","COPY",EDGE,{"derivedFrom":makeQuery(id+"F3.opExtrude","SWEPT_EDGE",EDGE,{"disambiguationData":[OSD([sQuery(id+"F0.wireOp",EDGE,"E0"),sQuery(id+"F0.wireOp",EDGE,"E1"),sQuery(id+"F2.wireOp",EDGE,"E12.14.1"),sQuery(id+"F2.wireOp",EDGE,"E12.14.2")])]})});
            var Q18;
            Q18=makeQuery(id+"F3.boolean.opBoolean","COPY",EDGE,{"derivedFrom":makeQuery(id+"F3.opExtrude","SWEPT_EDGE",EDGE,{"disambiguationData":[OSD([sQuery(id+"F0.wireOp",EDGE,"E0"),sQuery(id+"F0.wireOp",EDGE,"E1"),sQuery(id+"F2.wireOp",EDGE,"E12.13.0"),sQuery(id+"F2.wireOp",EDGE,"E12.13.1")])]})});
            var Q19;
            Q19=makeQuery(id+"F3.boolean.opBoolean","COPY",EDGE,{"derivedFrom":makeQuery(id+"F3.opExtrude","SWEPT_EDGE",EDGE,{"disambiguationData":[OSD([sQuery(id+"F0.wireOp",EDGE,"E0"),sQuery(id+"F0.wireOp",EDGE,"E1"),sQuery(id+"F2.wireOp",EDGE,"E12.13.1"),sQuery(id+"F2.wireOp",EDGE,"E12.13.2")])]})});
            var Q20;
            Q20=makeQuery(id+"F3.boolean.opBoolean","COPY",EDGE,{"derivedFrom":makeQuery(id+"F3.opExtrude","SWEPT_EDGE",EDGE,{"disambiguationData":[OSD([sQuery(id+"F0.wireOp",EDGE,"E0"),sQuery(id+"F0.wireOp",EDGE,"E1"),sQuery(id+"F2.wireOp",EDGE,"E12.12.1"),sQuery(id+"F2.wireOp",EDGE,"E12.12.2")])]})});
            var Q21;
            Q21=makeQuery(id+"F3.boolean.opBoolean","COPY",EDGE,{"derivedFrom":makeQuery(id+"F3.opExtrude","SWEPT_EDGE",EDGE,{"disambiguationData":[OSD([sQuery(id+"F0.wireOp",EDGE,"E0"),sQuery(id+"F0.wireOp",EDGE,"E1"),sQuery(id+"F2.wireOp",EDGE,"E12.12.0"),sQuery(id+"F2.wireOp",EDGE,"E12.12.1")])]})});
            var Q22;
            Q22=makeQuery(id+"F3.boolean.opBoolean","COPY",EDGE,{"derivedFrom":makeQuery(id+"F3.opExtrude","SWEPT_EDGE",EDGE,{"disambiguationData":[OSD([sQuery(id+"F0.wireOp",EDGE,"E0"),sQuery(id+"F0.wireOp",EDGE,"E1"),sQuery(id+"F2.wireOp",EDGE,"E12.11.0"),sQuery(id+"F2.wireOp",EDGE,"E12.11.1")])]})});
            var Q23;
            Q23=makeQuery(id+"F3.boolean.opBoolean","COPY",EDGE,{"derivedFrom":makeQuery(id+"F3.opExtrude","SWEPT_EDGE",EDGE,{"disambiguationData":[OSD([sQuery(id+"F0.wireOp",EDGE,"E0"),sQuery(id+"F0.wireOp",EDGE,"E1"),sQuery(id+"F2.wireOp",EDGE,"E12.11.1"),sQuery(id+"F2.wireOp",EDGE,"E12.11.2")])]})});
            var Q24;
            Q24=makeQuery(id+"F3.boolean.opBoolean","COPY",EDGE,{"derivedFrom":makeQuery(id+"F3.opExtrude","SWEPT_EDGE",EDGE,{"disambiguationData":[OSD([sQuery(id+"F0.wireOp",EDGE,"E0"),sQuery(id+"F0.wireOp",EDGE,"E1"),sQuery(id+"F2.wireOp",EDGE,"E12.10.0"),sQuery(id+"F2.wireOp",EDGE,"E12.10.1")])]})});
            var Q25;
            Q25=makeQuery(id+"F3.boolean.opBoolean","COPY",EDGE,{"derivedFrom":makeQuery(id+"F3.opExtrude","SWEPT_EDGE",EDGE,{"disambiguationData":[OSD([sQuery(id+"F0.wireOp",EDGE,"E0"),sQuery(id+"F0.wireOp",EDGE,"E1"),sQuery(id+"F2.wireOp",EDGE,"E12.10.1"),sQuery(id+"F2.wireOp",EDGE,"E12.10.2")])]})});
            var Q26;
            Q26=makeQuery(id+"F3.boolean.opBoolean","COPY",EDGE,{"derivedFrom":makeQuery(id+"F3.opExtrude","SWEPT_EDGE",EDGE,{"disambiguationData":[OSD([sQuery(id+"F0.wireOp",EDGE,"E0"),sQuery(id+"F0.wireOp",EDGE,"E1"),sQuery(id+"F2.wireOp",EDGE,"E12.9.0"),sQuery(id+"F2.wireOp",EDGE,"E12.9.1")])]})});
            var Q27;
            Q27=makeQuery(id+"F3.boolean.opBoolean","COPY",EDGE,{"derivedFrom":makeQuery(id+"F3.opExtrude","SWEPT_EDGE",EDGE,{"disambiguationData":[OSD([sQuery(id+"F0.wireOp",EDGE,"E0"),sQuery(id+"F0.wireOp",EDGE,"E1"),sQuery(id+"F2.wireOp",EDGE,"E12.9.1"),sQuery(id+"F2.wireOp",EDGE,"E12.9.2")])]})});
            var Q28;
            Q28=makeQuery(id+"F3.boolean.opBoolean","COPY",EDGE,{"derivedFrom":makeQuery(id+"F3.opExtrude","SWEPT_EDGE",EDGE,{"disambiguationData":[OSD([sQuery(id+"F0.wireOp",EDGE,"E0"),sQuery(id+"F0.wireOp",EDGE,"E1"),sQuery(id+"F2.wireOp",EDGE,"E12.8.0"),sQuery(id+"F2.wireOp",EDGE,"E12.8.1")])]})});
            var Q29;
            Q29=makeQuery(id+"F3.boolean.opBoolean","COPY",EDGE,{"derivedFrom":makeQuery(id+"F3.opExtrude","SWEPT_EDGE",EDGE,{"disambiguationData":[OSD([sQuery(id+"F0.wireOp",EDGE,"E0"),sQuery(id+"F0.wireOp",EDGE,"E1"),sQuery(id+"F2.wireOp",EDGE,"E12.8.1"),sQuery(id+"F2.wireOp",EDGE,"E12.8.2")])]})});
            var Q30;
            Q30=makeQuery(id+"F3.boolean.opBoolean","COPY",EDGE,{"derivedFrom":makeQuery(id+"F3.opExtrude","SWEPT_EDGE",EDGE,{"disambiguationData":[OSD([sQuery(id+"F0.wireOp",EDGE,"E0"),sQuery(id+"F0.wireOp",EDGE,"E1"),sQuery(id+"F2.wireOp",EDGE,"E12.7.0"),sQuery(id+"F2.wireOp",EDGE,"E12.7.1")])]})});
            var Q31;
            Q31=makeQuery(id+"F3.boolean.opBoolean","COPY",EDGE,{"derivedFrom":makeQuery(id+"F3.opExtrude","SWEPT_EDGE",EDGE,{"disambiguationData":[OSD([sQuery(id+"F0.wireOp",EDGE,"E0"),sQuery(id+"F0.wireOp",EDGE,"E1"),sQuery(id+"F2.wireOp",EDGE,"E12.7.1"),sQuery(id+"F2.wireOp",EDGE,"E12.7.2")])]})});
            var Q32;
            Q32=makeQuery(id+"F3.boolean.opBoolean","COPY",EDGE,{"derivedFrom":makeQuery(id+"F3.opExtrude","SWEPT_EDGE",EDGE,{"disambiguationData":[OSD([sQuery(id+"F0.wireOp",EDGE,"E0"),sQuery(id+"F0.wireOp",EDGE,"E1"),sQuery(id+"F2.wireOp",EDGE,"E12.6.0"),sQuery(id+"F2.wireOp",EDGE,"E12.6.1")])]})});
            var Q33;
            Q33=makeQuery(id+"F3.boolean.opBoolean","COPY",EDGE,{"derivedFrom":makeQuery(id+"F3.opExtrude","SWEPT_EDGE",EDGE,{"disambiguationData":[OSD([sQuery(id+"F0.wireOp",EDGE,"E0"),sQuery(id+"F0.wireOp",EDGE,"E1"),sQuery(id+"F2.wireOp",EDGE,"E12.6.1"),sQuery(id+"F2.wireOp",EDGE,"E12.6.2")])]})});
            var Q34;
            Q34=makeQuery(id+"F3.boolean.opBoolean","COPY",EDGE,{"derivedFrom":makeQuery(id+"F3.opExtrude","SWEPT_EDGE",EDGE,{"disambiguationData":[OSD([sQuery(id+"F0.wireOp",EDGE,"E0"),sQuery(id+"F0.wireOp",EDGE,"E1"),sQuery(id+"F2.wireOp",EDGE,"E12.5.0"),sQuery(id+"F2.wireOp",EDGE,"E12.5.1")])]})});
            var Q35;
            Q35=makeQuery(id+"F3.boolean.opBoolean","COPY",EDGE,{"derivedFrom":makeQuery(id+"F3.opExtrude","SWEPT_EDGE",EDGE,{"disambiguationData":[OSD([sQuery(id+"F0.wireOp",EDGE,"E0"),sQuery(id+"F0.wireOp",EDGE,"E1"),sQuery(id+"F2.wireOp",EDGE,"E12.5.1"),sQuery(id+"F2.wireOp",EDGE,"E12.5.2")])]})});
            var Q36;
            Q36=makeQuery(id+"F3.boolean.opBoolean","COPY",EDGE,{"derivedFrom":makeQuery(id+"F3.opExtrude","SWEPT_EDGE",EDGE,{"disambiguationData":[OSD([sQuery(id+"F0.wireOp",EDGE,"E0"),sQuery(id+"F0.wireOp",EDGE,"E1"),sQuery(id+"F2.wireOp",EDGE,"E12.4.0"),sQuery(id+"F2.wireOp",EDGE,"E12.4.1")])]})});
            var Q37;
            Q37=makeQuery(id+"F3.boolean.opBoolean","COPY",EDGE,{"derivedFrom":makeQuery(id+"F3.opExtrude","SWEPT_EDGE",EDGE,{"disambiguationData":[OSD([sQuery(id+"F0.wireOp",EDGE,"E0"),sQuery(id+"F0.wireOp",EDGE,"E1"),sQuery(id+"F2.wireOp",EDGE,"E12.4.1"),sQuery(id+"F2.wireOp",EDGE,"E12.4.2")])]})});
            var Q38;
            Q38=makeQuery(id+"F3.boolean.opBoolean","COPY",EDGE,{"derivedFrom":makeQuery(id+"F3.opExtrude","SWEPT_EDGE",EDGE,{"disambiguationData":[OSD([sQuery(id+"F0.wireOp",EDGE,"E0"),sQuery(id+"F0.wireOp",EDGE,"E1"),sQuery(id+"F2.wireOp",EDGE,"E12.3.0"),sQuery(id+"F2.wireOp",EDGE,"E12.3.1")])]})});
            var Q39;
            Q39=makeQuery(id+"F3.boolean.opBoolean","COPY",EDGE,{"derivedFrom":makeQuery(id+"F3.opExtrude","SWEPT_EDGE",EDGE,{"disambiguationData":[OSD([sQuery(id+"F0.wireOp",EDGE,"E0"),sQuery(id+"F0.wireOp",EDGE,"E1"),sQuery(id+"F2.wireOp",EDGE,"E12.3.1"),sQuery(id+"F2.wireOp",EDGE,"E12.3.2")])]})});
            var Q40;
            Q40=makeQuery(id+"F3.boolean.opBoolean","COPY",EDGE,{"derivedFrom":makeQuery(id+"F3.opExtrude","SWEPT_EDGE",EDGE,{"disambiguationData":[OSD([sQuery(id+"F0.wireOp",EDGE,"E0"),sQuery(id+"F0.wireOp",EDGE,"E1"),sQuery(id+"F2.wireOp",EDGE,"E12.2.0"),sQuery(id+"F2.wireOp",EDGE,"E12.2.1")])]})});
            var Q41;
            Q41=makeQuery(id+"F3.boolean.opBoolean","COPY",EDGE,{"derivedFrom":makeQuery(id+"F3.opExtrude","SWEPT_EDGE",EDGE,{"disambiguationData":[OSD([sQuery(id+"F0.wireOp",EDGE,"E0"),sQuery(id+"F0.wireOp",EDGE,"E1"),sQuery(id+"F2.wireOp",EDGE,"E12.2.1"),sQuery(id+"F2.wireOp",EDGE,"E12.2.2")])]})});
            var Q42;
            Q42=makeQuery(id+"F3.boolean.opBoolean","COPY",EDGE,{"derivedFrom":makeQuery(id+"F3.opExtrude","SWEPT_EDGE",EDGE,{"disambiguationData":[OSD([sQuery(id+"F0.wireOp",EDGE,"E0"),sQuery(id+"F0.wireOp",EDGE,"E1"),sQuery(id+"F2.wireOp",EDGE,"E12.1.0"),sQuery(id+"F2.wireOp",EDGE,"E12.1.1")])]})});
            var Q43;
            Q43=makeQuery(id+"F3.boolean.opBoolean","COPY",EDGE,{"derivedFrom":makeQuery(id+"F3.opExtrude","SWEPT_EDGE",EDGE,{"disambiguationData":[OSD([sQuery(id+"F0.wireOp",EDGE,"E0"),sQuery(id+"F0.wireOp",EDGE,"E1"),sQuery(id+"F2.wireOp",EDGE,"E12.1.1"),sQuery(id+"F2.wireOp",EDGE,"E12.1.2")])]})});
            var Q44;
            Q44=makeQuery(id+"F3.boolean.opBoolean","COPY",EDGE,{"derivedFrom":makeQuery(id+"F3.opExtrude","SWEPT_EDGE",EDGE,{"disambiguationData":[OSD([sQuery(id+"F0.wireOp",EDGE,"E0"),sQuery(id+"F0.wireOp",EDGE,"E1"),sQuery(id+"F2.wireOp",EDGE,"E10"),sQuery(id+"F2.wireOp",EDGE,"E11.MirrorCS")])]})});
            var Q45;
            Q45=makeQuery(id+"F3.boolean.opBoolean","COPY",EDGE,{"derivedFrom":makeQuery(id+"F3.opExtrude","SWEPT_EDGE",EDGE,{"disambiguationData":[OSD([sQuery(id+"F0.wireOp",EDGE,"E0"),sQuery(id+"F0.wireOp",EDGE,"E1"),sQuery(id+"F2.wireOp",EDGE,"E9"),sQuery(id+"F2.wireOp",EDGE,"E10")])]})});
            var Q46;
            Q46=makeQuery(id+"F3.boolean.opBoolean","COPY",EDGE,{"derivedFrom":makeQuery(id+"F3.opExtrude","SWEPT_EDGE",EDGE,{"disambiguationData":[OSD([sQuery(id+"F0.wireOp",EDGE,"E0"),sQuery(id+"F0.wireOp",EDGE,"E1"),sQuery(id+"F2.wireOp",EDGE,"E12.23.0"),sQuery(id+"F2.wireOp",EDGE,"E12.23.1")])]})});
            var Q47;
            Q47=makeQuery(id+"F3.boolean.opBoolean","COPY",EDGE,{"derivedFrom":makeQuery(id+"F3.opExtrude","SWEPT_EDGE",EDGE,{"disambiguationData":[OSD([sQuery(id+"F0.wireOp",EDGE,"E0"),sQuery(id+"F0.wireOp",EDGE,"E1"),sQuery(id+"F2.wireOp",EDGE,"E12.23.1"),sQuery(id+"F2.wireOp",EDGE,"E12.23.2")])]})});
            fillet(context, id + "F5", {"entities" : qUnion([Q0, Q1, Q2, Q3, Q4, Q5, Q6, Q7, Q8, Q9, Q10, Q11, Q12, Q13, Q14, Q15, Q16, Q17, Q18, Q19, Q20, Q21, Q22, Q23, Q24, Q25, Q26, Q27, Q28, Q29, Q30, Q31, Q32, Q33, Q34, Q35, Q36, Q37, Q38, Q39, Q40, Q41, Q42, Q43, Q44, Q45, Q46, Q47]), "radius" : 0.2 * mm, "tangentPropagation" : true, "allowEdgeOverflow" : false});
        }
        {
            var Q0;
            Q0=makeQuery(id+"F1.opRevolve","SWEPT_EDGE",EDGE,{"disambiguationData":[OSD([sQuery(id+"F0.wireOp",EDGE,"E2"),sQuery(id+"F0.wireOp",EDGE,"E3")])]});
            var Q1;
            Q1=makeQuery(id+"F1.opRevolve","SWEPT_EDGE",EDGE,{"disambiguationData":[OSD([sQuery(id+"F0.wireOp",EDGE,"E4"),sQuery(id+"F0.wireOp",EDGE,"E5")])]});
            fillet(context, id + "F6", {"entities" : qUnion([Q0, Q1]), "radius" : 0.2 * mm, "tangentPropagation" : true, "allowEdgeOverflow" : false});
        }
        {
            var Q0;
            Q0=makeQuery(id+"F1.opRevolve","SWEPT_EDGE",EDGE,{"disambiguationData":[OSD([sQuery(id+"F0.wireOp",EDGE,"E5"),sQuery(id+"F0.wireOp",EDGE,"E6")])]});
            var Q1;
            Q1=makeQuery(id+"F1.opRevolve","SWEPT_EDGE",EDGE,{"disambiguationData":[OSD([sQuery(id+"F0.wireOp",EDGE,"E3"),sQuery(id+"F0.wireOp",EDGE,"E4")])]});
            chamfer(context, id + "F7", {"entities" : qUnion([Q0, Q1]), "width" : 0.2 * mm, "tangentPropagation" : true});
        }
    });
